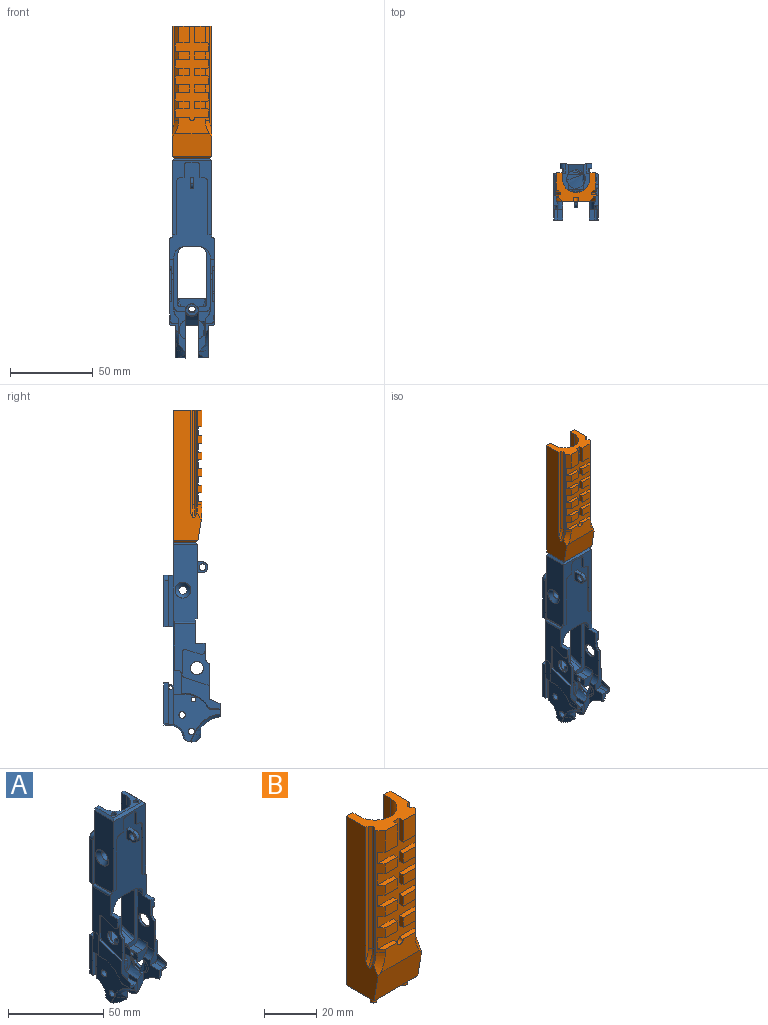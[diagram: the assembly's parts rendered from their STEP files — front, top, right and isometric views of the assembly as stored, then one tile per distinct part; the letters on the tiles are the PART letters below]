
ASSEMBLY  parts=2 mates=1
PART A: 257 faces, bbox 27.3x36.3x122.7 mm
  f0: plane 2.29x2.29mm, normal (0,0,-1), area 4.1mm2, adj f3
  f1: revolved ~2.45x2.45mm, area 5.5mm2, adj f7
  f2: plane 3.88x1.52mm, normal (0,-0.31,0.95), area 4.5mm2, adj f4,f9,f11,f15
  f3: revolved ~4.48x2.29mm, area 64.4mm2, adj f0,f16
  f4: revolved ~8.5x8.5mm, area 11.2mm2, adj f2,f11,f12,f15,f18,f21
  f5: plane 0.09x0.09mm, normal (0,-1,0), area 0mm2, adj f6,f20,f21
  f6: bspline ~6.22x2.03mm, area 0.6mm2, adj f5,f20,f21,f71
  f7: revolved ~2.74x2.45mm, area 42.1mm2, adj f1,f29
  f8: revolved ~4.17x4.17mm, area 7.3mm2, adj f28,f33
  f9: revolved ~8.3x5.57mm, area 28.9mm2, adj f2,f11,f15,f18,f35
  f10: plane 11.64x3.81mm, normal (0,-1,0), area 32mm2, adj f11,f35
  f11: revolved ~11.64x8.89mm, area 51.2mm2, adj f2,f4,f9,f10,f12,f35
  f12: plane 10.47x4.14mm, normal (0,-1,0), area 29.5mm2, adj f4,f11,f14,f20,f21,f35
  f13: plane 5.19x2.18mm, normal (0,-0.92,-0.39), area 0mm2, adj f14,f41
  f14: revolved ~6.77x5.98mm, area 26.7mm2, adj f12,f13,f20,f35,f42
  f15: plane 12.35x9.78mm, normal (-1,0,0), area 36.3mm2, adj f2,f4,f9,f18,f43,f44,f45,f46
  f16: plane 2.8x2.8mm, normal (0,0,-1), area 2mm2, adj f3,f51
  f17: revolved ~2.34x1.3mm, area 1.8mm2, adj f18,f35,f54
  f18: plane 4.58x4.03mm, normal (0,0.31,-0.95), area 12.7mm2, adj f4,f9,f15,f17,f21,f35,f54
  f19: plane 21.92x16.23mm, normal (1,0,0), area 223.2mm2, adj f52,f55,f62,f63,f64,f65,f66,f67
  f20: bspline ~15.82x13.1mm, area 51.2mm2, adj f5,f6,f12,f14,f21,f41,f71
  f21: plane 15.59x11.71mm, normal (-1,0,0), area 86.1mm2, adj f4,f5,f6,f12,f18,f20,f22,f53
  f22: plane 6.6x3.43mm, normal (0,0,1), area 22.6mm2, adj f21,f23,f69,f71
  f23: revolved ~6.6x1.59mm, area 16.5mm2, adj f22,f24,f69,f71
  f24: plane 6.6x3.63mm, normal (-1,0,0), area 14.7mm2, adj f23,f69,f70,f71
  f25: plane 0.09x0.09mm, normal (0,-1,0), area 0mm2, adj f26,f80,f81
  f26: bspline ~6.22x2.03mm, area 0.6mm2, adj f25,f80,f81,f144
  f27: revolved ~3.18x3.18mm, area 9.2mm2, adj f91
  f28: revolved ~5.17x4.64mm, area 59.5mm2, adj f8,f92
  f29: revolved ~2.96x2.96mm, area 4.3mm2, adj f7,f92
  f30: revolved ~3.68x3.68mm, area 5.5mm2, adj f91,f92
  f31: plane 2.54x0.16mm, normal (0,0.06,-1), area 0.3mm2, adj f36,f92,f93,f94
  f32: plane 21.91x16.23mm, normal (-1,0,0), area 223.2mm2, adj f56,f57,f104,f105,f106,f107,f108,f109
  f33: plane 7.97x7.9mm, normal (0,-0.99,-0.1), area 35.9mm2, adj f8,f88,f90,f114
  f34: plane 1.64x0.17mm, normal (0,-0.06,1), area 0.3mm2, adj f36,f37,f94,f118
  f35: plane 28.3x22.24mm, normal (-1,0,0), area 324.2mm2, adj f9,f10,f11,f12,f14,f17,f18,f36
  f36: revolved ~5.6x4.24mm, area 21mm2, adj f31,f34,f35,f92,f94,f119
  f37: bspline ~1.39x0.2mm, area 0.2mm2, adj f34,f118,f119,f194
  f38: revolved ~3.14x2.2mm, area 8.4mm2, adj f39,f50,f73,f121
  f39: plane 5.22x3.14mm, normal (0,0,-1), area 16.4mm2, adj f38,f71,f72,f121
  f40: revolved ~5.93x3.96mm, area 73.7mm2, adj f35,f41,f121
  f41: bspline ~17.88x17.13mm, area 10.9mm2, adj f13,f20,f40,f42,f71,f121
  f42: revolved ~10.38x5.93mm, area 47.7mm2, adj f14,f35,f41,f119,f120,f121
  f43: revolved ~5.2x3.49mm, area 13.3mm2, adj f15,f44,f47,f121
  f44: plane 4.69x1.59mm, normal (0,-0.31,0.95), area 7.8mm2, adj f15,f43,f45,f121
  f45: revolved ~4.76x3.49mm, area 11.8mm2, adj f15,f44,f46,f121
  f46: revolved ~5.22x2.62mm, area 10.6mm2, adj f15,f45,f47,f121
  f47: plane 1.59x0.3mm, normal (0,0.31,-0.95), area 0.5mm2, adj f15,f43,f46,f121
  f48: revolved ~5.93x2.79mm, area 104.1mm2, adj f35,f121
  f49: revolved ~5.93x4mm, area 74.5mm2, adj f35,f121
  f50: revolved ~13.78x7.99mm, area 52.3mm2, adj f38,f53,f54,f74,f121,f122
  f51: revolved ~26.67x2.79mm, area 234.1mm2, adj f16,f122
  f52: revolved ~3.68x2.44mm, area 6.1mm2, adj f19,f62,f69,f125
  f53: revolved ~5.32x5.08mm, area 32mm2, adj f21,f50,f54,f69,f121,f125
  f54: plane 9.02x7.01mm, normal (0,-1,0), area 33.2mm2, adj f17,f18,f21,f35,f50,f53,f114,f115
  f55: revolved ~7.95x7.95mm, area 32.7mm2, adj f19,f125
  f56: revolved ~3.68x2.44mm, area 6.1mm2, adj f32,f104,f111,f126
  f57: revolved ~7.95x7.95mm, area 32.7mm2, adj f32,f126
  f58: revolved ~3.18x3.18mm, area 11.7mm2, adj f59,f129,f130,f131
  f59: revolved ~3.18x3.18mm, area 11.7mm2, adj f58,f128,f129,f131
  f60: revolved ~4.04x4.04mm, area 29.6mm2, adj f129,f131
  f61: plane 7.14x0.51mm, normal (0.71,0,-0.71), area 4.9mm2, adj f74,f122,f123,f132
  f62: plane 8.51x2.57mm, normal (0,-1,0), area 16.8mm2, adj f19,f52,f63,f124,f125,f132
  f63: revolved ~4.57x4.55mm, area 23.5mm2, adj f19,f62,f64,f132
  f64: plane 8.72x2.83mm, normal (0,0.31,-0.95), area 11.5mm2, adj f19,f63,f65,f132
  f65: revolved ~2.08x1.59mm, area 3.8mm2, adj f19,f64,f66,f132
  f66: plane 13.89x1.26mm, normal (0,-1,0), area 17.5mm2, adj f19,f65,f67,f132
  f67: revolved ~1.51x1.26mm, area 2.5mm2, adj f19,f66,f68,f132
  f68: plane 15.13x4.92mm, normal (0,-0.31,0.95), area 20mm2, adj f19,f67,f69,f132
  f69: plane 26.8x5.45mm, normal (0,-1,0), area 62.3mm2, adj f19,f21,f22,f23,f24,f52,f53,f68
  f70: plane 6.6x2.8mm, normal (0,-0.39,0.92), area 3.1mm2, adj f24,f69,f71,f132
  f71: plane 8.06x5.46mm, normal (0,-1,0), area 14.2mm2, adj f6,f20,f21,f22,f23,f24,f39,f41
  f72: plane 5.22x0.51mm, normal (0.71,0,-0.71), area 3.8mm2, adj f39,f71,f73,f132
  f73: revolved ~2.2x1.53mm, area 1.7mm2, adj f38,f72,f74,f132
  f74: revolved ~14.22x8.5mm, area 12.2mm2, adj f50,f61,f73,f132
  f75: revolved ~5.32x5.08mm, area 32mm2, adj f80,f104,f126,f141,f147,f218
  f76: plane 5.19x2.18mm, normal (0,-0.92,-0.39), area 0mm2, adj f87,f143,f152
  f77: plane 6.6x3.63mm, normal (1,0,0), area 14.7mm2, adj f78,f103,f104,f144
  f78: revolved ~6.6x1.59mm, area 16.5mm2, adj f77,f79,f104,f144
  f79: plane 6.6x3.43mm, normal (0,0,1), area 22.6mm2, adj f78,f80,f104,f144
  f80: plane 15.59x11.71mm, normal (1,0,0), area 109mm2, adj f25,f26,f75,f79,f81,f104,f141,f144
  f81: bspline ~15.82x13.1mm, area 51.2mm2, adj f25,f26,f80,f87,f141,f143,f144
  f82: plane 2.54x0.16mm, normal (0,0.06,-1), area 0.3mm2, adj f92,f95,f150,f158
  f83: revolved ~9.49x8.73mm, area 81.8mm2, adj f35,f86,f114,f151
  f84: plane 11.64x3.81mm, normal (0,-1,0), area 32mm2, adj f85,f151
  f85: revolved ~11.64x8.89mm, area 130.9mm2, adj f84,f141,f151
  f86: plane 7.87x1.38mm, normal (0,0,-1), area 10.9mm2, adj f35,f83,f92,f151
  f87: revolved ~6.77x5.98mm, area 26.7mm2, adj f76,f81,f141,f151,f152
  f88: revolved ~1.99x0.92mm, area 0.1mm2, adj f33,f89,f155
  f89: plane 5.19x0.92mm, normal (0,0.99,0.1), area 3.4mm2, adj f88,f90,f155
  f90: revolved ~1.99x0.92mm, area 0.1mm2, adj f33,f89,f155
  f91: revolved ~7.94x3.18mm, area 72mm2, adj f27,f30,f155
  f92: plane 25.55x19.4mm, normal (0,1,0), area 383.5mm2, adj f28,f29,f30,f31,f35,f36,f82,f86
  f93: plane 24.86x2.54mm, normal (1,0,0), area 62.9mm2, adj f31,f92,f94,f157
  f94: plane 25.15x1.86mm, normal (0,-1,0), area 45.9mm2, adj f31,f34,f36,f93,f117,f118,f157
  f95: plane 24.86x2.54mm, normal (-1,0,0), area 62.9mm2, adj f82,f92,f157,f158
  f96: plane 6.99x3.84mm, normal (0,0,1), area 26.6mm2, adj f99,f114,f141,f162
  f97: plane 2.97x1.89mm, normal (1,0,0), area 2.9mm2, adj f98,f114,f162
  f98: revolved ~2.97x1.57mm, area 1.3mm2, adj f97,f114,f162
  f99: revolved ~6.99x3.18mm, area 34.8mm2, adj f96,f126,f141,f162
  f100: revolved ~14.22x8.5mm, area 12.2mm2, adj f101,f140,f147,f167
  f101: revolved ~2.2x1.53mm, area 1.7mm2, adj f100,f102,f146,f167
  f102: plane 5.22x0.51mm, normal (-0.71,0,-0.71), area 3.8mm2, adj f101,f144,f145,f167
  f103: plane 6.6x2.8mm, normal (0,-0.39,0.92), area 3.1mm2, adj f77,f104,f144,f167
  f104: plane 26.8x5.45mm, normal (0,-1,0), area 62.3mm2, adj f32,f56,f75,f77,f78,f79,f80,f103
  f105: plane 15.13x4.92mm, normal (0,-0.31,0.95), area 20mm2, adj f32,f104,f106,f167
  f106: revolved ~1.51x1.26mm, area 2.5mm2, adj f32,f105,f107,f167
  f107: plane 13.89x1.26mm, normal (0,-1,0), area 17.5mm2, adj f32,f106,f108,f167
  f108: revolved ~2.08x1.59mm, area 3.8mm2, adj f32,f107,f109,f167
  f109: plane 8.72x2.83mm, normal (0,0.31,-0.95), area 11.5mm2, adj f32,f108,f110,f167
  f110: revolved ~2.99x2.29mm, area 5.4mm2, adj f32,f109,f111,f167
  f111: plane 8.51x2.57mm, normal (0,-1,0), area 16.8mm2, adj f32,f56,f110,f126,f127,f167
  f112: revolved ~2.97x1.57mm, area 1.3mm2, adj f113,f114,f188
  f113: plane 2.97x1.89mm, normal (-1,0,0), area 2.9mm2, adj f112,f114,f188
  f114: revolved ~18.31x9.73mm, area 158.1mm2, adj f33,f35,f54,f83,f96,f97,f98,f112
  f115: plane 6.99x3.84mm, normal (0,0,1), area 26.6mm2, adj f54,f114,f116,f188
  f116: revolved ~6.99x3.18mm, area 34.8mm2, adj f54,f115,f125,f188
  f117: revolved ~15.25x6.17mm, area 29.5mm2, adj f94,f118,f156,f157,f187,f188,f194
  f118: plane 24.96x3.04mm, normal (1,0,0), area 69mm2, adj f34,f37,f94,f117,f155,f194
  f119: bspline ~9.13x8.49mm, area 68.2mm2, adj f35,f36,f37,f42,f120,f194
  f120: revolved ~8.86x6.86mm, area 4mm2, adj f42,f119,f121,f194
  f121: plane 28.95x28.4mm, normal (1,0,0), area 358.4mm2, adj f38,f39,f40,f41,f42,f43,f44,f45
  f122: plane 7.14x3.14mm, normal (0,0,-1), area 16.3mm2, adj f50,f51,f61,f121,f194
  f123: plane 31.7x0.51mm, normal (0.71,0.71,0), area 22.6mm2, adj f61,f132,f194,f198
  f124: plane 5.82x2.57mm, normal (0,0,1), area 14.9mm2, adj f62,f125,f132,f201
  f125: plane 32.09x12.07mm, normal (-1,0,0), area 283.8mm2, adj f52,f53,f54,f55,f62,f69,f116,f124
  f126: plane 32.09x12.07mm, normal (1,0,0), area 283.8mm2, adj f56,f57,f75,f99,f104,f111,f127,f141
  f127: plane 5.82x2.57mm, normal (0,0,1), area 14.9mm2, adj f111,f126,f167,f201
  f128: plane 4.32x2.34mm, normal (0,0,1), area 10.1mm2, adj f59,f129,f131,f201
  f129: plane 7.5x6.35mm, normal (-1,0,0), area 30.4mm2, adj f58,f59,f60,f128,f130,f201
  f130: plane 4.32x2.34mm, normal (0,0,-1), area 10.1mm2, adj f58,f129,f131,f201
  f131: plane 7.5x6.35mm, normal (1,0,0), area 30.4mm2, adj f58,f59,f60,f128,f130,f201
  f132: plane 51.57x27.84mm, normal (1,0,0), area 473.8mm2, adj f61,f62,f63,f64,f65,f66,f67,f68
  f133: revolved ~4.27x1.27mm, area 8.4mm2, adj f132,f201,f202,f203
  f134: plane 5.93x0.85mm, normal (0,0,1), area 3.4mm2, adj f210,f211
  f135: revolved ~6.35x6.33mm, area 26.6mm2, adj f212,f213,f214,f215
  f136: plane 9.47x1.91mm, normal (0,0.71,0.71), area 25.5mm2, adj f137,f192,f211,f216
  f137: plane 9.47x6.1mm, normal (0,0,1), area 57.8mm2, adj f136,f211,f215,f216
  f138: plane 5.93x0.85mm, normal (0,0,1), area 3.4mm2, adj f205,f216
  f139: revolved ~5.11x5.11mm, area 78mm2, adj f171,f216
  f140: plane 2.31x0.51mm, normal (-0.71,0,-0.71), area 1.7mm2, adj f100,f167,f169,f217
  f141: plane 27.95x7.02mm, normal (0,-1,0), area 70.4mm2, adj f75,f80,f81,f85,f87,f96,f99,f114
  f142: revolved ~5.93x3.96mm, area 73.7mm2, adj f143,f151,f218
  f143: bspline ~18.1x17.29mm, area 10.9mm2, adj f76,f81,f142,f144,f152,f218
  f144: plane 8.06x5.46mm, normal (0,-1,0), area 14.2mm2, adj f26,f77,f78,f79,f80,f81,f102,f103
  f145: plane 5.22x3.14mm, normal (0,0,-1), area 16.4mm2, adj f102,f144,f146,f218
  f146: revolved ~3.14x2.2mm, area 8.4mm2, adj f101,f145,f147,f218
  f147: revolved ~13.78x7.99mm, area 52.3mm2, adj f75,f100,f141,f146,f217,f218
  f148: revolved ~5.93x4mm, area 74.5mm2, adj f151,f218
  f149: revolved ~5.93x2.79mm, area 52.1mm2, adj f151,f218
  f150: revolved ~5.6x4.24mm, area 21mm2, adj f82,f92,f151,f153,f158,f220
  f151: plane 28.3x22.24mm, normal (1,0,0), area 325.4mm2, adj f83,f84,f85,f86,f87,f92,f114,f141
  f152: revolved ~10.38x5.93mm, area 48mm2, adj f76,f87,f143,f151,f218,f219,f220
  f153: plane 1.64x0.17mm, normal (0,-0.06,1), area 0.3mm2, adj f150,f154,f158,f221
  f154: bspline ~1.39x0.2mm, area 0.2mm2, adj f153,f220,f221,f245
  f155: revolved ~15.62x2.36mm, area 104.7mm2, adj f88,f89,f90,f91,f114,f118,f221
  f156: plane 14.78x14.28mm, normal (0,-0.3,0.95), area 197.1mm2, adj f114,f117,f157,f162,f188,f222
  f157: plane 19.3x2.54mm, normal (0,0,1), area 15.7mm2, adj f92,f93,f94,f95,f117,f156,f158,f222
  f158: plane 25.15x1.86mm, normal (0,-1,0), area 45.9mm2, adj f82,f95,f150,f153,f157,f221,f222
  f159: revolved ~0.31x0.26mm, area 0mm2, adj f206,f216,f224
  f160: plane 1.5x1.42mm, normal (0,0,-1), area 0.7mm2, adj f161,f201,f224
  f161: revolved ~6.03x6.03mm, area 34.2mm2, adj f126,f160,f162,f201,f224
  f162: plane 39.26x8.3mm, normal (0,-1,0), area 96.8mm2, adj f96,f97,f98,f99,f114,f126,f156,f161
  f163: plane 30.87x1.84mm, normal (0,-1,0), area 55.5mm2, adj f164,f165,f225,f226,f227
  f164: plane 28.07x2.54mm, normal (-1,0,0), area 71.3mm2, adj f163,f207,f225,f227
  f165: plane 3.02x0.17mm, normal (0,0,-1), area 0.5mm2, adj f163,f226,f227,f245
  f166: revolved ~12.98x1.27mm, area 25.9mm2, adj f167,f170,f201,f229
  f167: plane 51.57x27.84mm, normal (-1,0,0), area 506.7mm2, adj f100,f101,f102,f103,f104,f105,f106,f107
  f168: revolved ~1.59x1.59mm, area 2.2mm2, adj f167,f169,f231,f232
  f169: plane 12.76x0.89mm, normal (0,1,0), area 11.2mm2, adj f140,f167,f168,f217,f232
  f170: plane 12.98x0.43mm, normal (0,0,1), area 5.6mm2, adj f166,f201,f228,f233
  f171: revolved ~9.53x9.53mm, area 71.8mm2, adj f139,f233
  f172: plane 31.5x1.12mm, normal (-1,0,0), area 35.2mm2, adj f173,f200,f201,f234
  f173: revolved ~3.18x3.18mm, area 5.6mm2, adj f172,f174,f201,f234
  f174: plane 1.71x1.12mm, normal (0,0,-1), area 1.9mm2, adj f173,f175,f201,f234
  f175: plane 7.3x1.12mm, normal (-1,0,0), area 8.2mm2, adj f174,f176,f201,f234
  f176: revolved ~1.59x1.59mm, area 2.8mm2, adj f175,f177,f201,f234
  f177: plane 6.35x1.12mm, normal (0,0,-1), area 7.1mm2, adj f176,f178,f201,f234
  f178: revolved ~1.59x1.59mm, area 2.8mm2, adj f177,f179,f201,f234
  f179: plane 7.3x1.12mm, normal (1,0,0), area 8.2mm2, adj f178,f180,f201,f234
  f180: plane 1.71x1.12mm, normal (0,0,-1), area 1.9mm2, adj f179,f181,f201,f234
  f181: revolved ~3.18x3.18mm, area 5.6mm2, adj f180,f182,f201,f234
  f182: plane 31.5x1.12mm, normal (1,0,0), area 35.2mm2, adj f181,f183,f201,f234
  f183: plane 2.16x1.12mm, normal (0,0,-1), area 2.4mm2, adj f182,f201,f233,f234
  f184: plane 3.02x0.17mm, normal (0,0,-1), area 0.5mm2, adj f185,f235,f236,f249
  f185: plane 30.87x1.84mm, normal (0,-1,0), area 55.5mm2, adj f184,f186,f235,f236,f237
  f186: plane 28.07x2.54mm, normal (1,0,0), area 71.3mm2, adj f185,f208,f235,f237
  f187: plane 30.43x9.68mm, normal (-1,0,0), area 265.5mm2, adj f117,f188,f194,f195,f196,f238
  f188: plane 39.26x8.3mm, normal (0,-1,0), area 96.8mm2, adj f112,f113,f114,f115,f116,f117,f125,f156
  f189: revolved ~6.03x6.03mm, area 34.2mm2, adj f125,f188,f190,f201,f238
  f190: plane 1.5x1.42mm, normal (0,0,-1), area 0.7mm2, adj f189,f201,f238
  f191: plane 11.43x4.75mm, normal (0,0.3,-0.95), area 56.9mm2, adj f192,f201,f224,f238
  f192: plane 9.55x4.37mm, normal (0,1,0), area 36.9mm2, adj f136,f191,f211,f216,f224,f238
  f193: revolved ~0.31x0.26mm, area 0mm2, adj f209,f211,f238
  f194: plane 50.92x5.28mm, normal (0,1,0), area 179.4mm2, adj f37,f117,f118,f119,f120,f121,f122,f123
  f195: plane 5.87x0.76mm, normal (0,0,1), area 4.5mm2, adj f187,f194,f196,f240
  f196: plane 6.73x2.61mm, normal (0,1,0), area 7.5mm2, adj f187,f195,f238,f239,f240
  f197: revolved ~4.03x1.58mm, area 9.6mm2, adj f132,f198,f203,f240
  f198: plane 6.96x4.03mm, normal (0,0,1), area 27.9mm2, adj f123,f132,f194,f197,f240
  f199: revolved ~5.11x5.11mm, area 76.2mm2, adj f211,f240
  f200: plane 2.16x1.12mm, normal (0,0,-1), area 2.4mm2, adj f172,f201,f234,f242
  f201: plane 58.44x27.05mm, normal (0,-1,0), area 979.5mm2, adj f124,f125,f126,f127,f128,f129,f130,f131
  f202: plane 4.18x0.43mm, normal (0,0,1), area 1.8mm2, adj f133,f201,f203,f242
  f203: plane 29.06x4.07mm, normal (0,1,0.07), area 85.9mm2, adj f132,f133,f197,f202,f204,f240,f242
  f204: revolved ~6.79x6.35mm, area 24.2mm2, adj f203,f240,f241,f242
  f205: revolved ~5.93x3.81mm, area 23.8mm2, adj f138,f216,f243
  f206: revolved ~28.34x0.81mm, area 28.1mm2, adj f159,f207,f216,f224,f243
  f207: plane 31.37x4.23mm, normal (0,1,0), area 121.7mm2, adj f164,f206,f224,f225,f227,f243
  f208: plane 31.37x4.23mm, normal (0,1,0), area 121.7mm2, adj f186,f209,f235,f237,f238,f243
  f209: revolved ~28.34x0.81mm, area 28.1mm2, adj f193,f208,f211,f238,f243
  f210: revolved ~5.93x3.81mm, area 23.8mm2, adj f134,f211,f243
  f211: plane 30.34x15.04mm, normal (-1,0,0), area 357.6mm2, adj f134,f136,f137,f192,f193,f199,f209,f210
  f212: plane 13.78x0.89mm, normal (-1,0,0), area 12.2mm2, adj f135,f213,f215,f243
  f213: plane 16.96x6.35mm, normal (0,1,0), area 103.3mm2, adj f135,f212,f214,f243
  f214: plane 13.78x0.89mm, normal (1,0,0), area 12.2mm2, adj f135,f213,f215,f243
  f215: plane 24.13x9.48mm, normal (0,1,0), area 125.3mm2, adj f135,f137,f211,f212,f214,f216,f243
  f216: plane 30.34x15.04mm, normal (1,0,0), area 357.6mm2, adj f136,f137,f138,f139,f159,f192,f205,f206
  f217: plane 7.14x3.14mm, normal (0,0,-1), area 20.6mm2, adj f140,f147,f169,f218,f232,f245
  f218: plane 28.95x28.4mm, normal (-1,0,0), area 413.9mm2, adj f75,f141,f142,f143,f144,f145,f146,f147
  f219: revolved ~8.86x6.86mm, area 4mm2, adj f152,f218,f220,f245
  f220: bspline ~9.06x8.27mm, area 68.2mm2, adj f150,f151,f152,f154,f219,f245
  f221: plane 24.96x3.04mm, normal (-1,0,0), area 69mm2, adj f153,f154,f155,f158,f222,f245
  f222: revolved ~15.25x6.17mm, area 29.5mm2, adj f156,f157,f158,f162,f221,f223,f245
  f223: plane 32.28x9.68mm, normal (1,0,0), area 282.9mm2, adj f162,f222,f224,f245
  f224: revolved ~20.75x12mm, area 129.2mm2, adj f159,f160,f161,f162,f191,f192,f201,f206
  f225: plane 5.86x3.01mm, normal (0,0,-1), area 5.9mm2, adj f163,f164,f207,f224,f226,f245
  f226: plane 30.87x3.02mm, normal (-1,0,0), area 93.3mm2, adj f163,f165,f225,f245
  f227: revolved ~5.56x3.18mm, area 17.4mm2, adj f163,f164,f165,f207,f243,f245
  f228: plane 0.51x0.51mm, normal (0,0.71,0.71), area 0.3mm2, adj f170,f229,f233,f245
  f229: revolved ~1.27x1.27mm, area 1.1mm2, adj f166,f228,f230,f245
  f230: plane 28.45x0.51mm, normal (-0.71,0.71,0), area 20.4mm2, adj f167,f229,f231,f245
  f231: plane 3.24x0.89mm, normal (0,0,-1), area 2.7mm2, adj f167,f168,f230,f232,f245
  f232: plane 14.35x4.83mm, normal (-1,0,0), area 68.7mm2, adj f168,f169,f217,f231,f245
  f233: plane 46.99x14.61mm, normal (-1,0,0), area 605.9mm2, adj f170,f171,f183,f201,f228,f234,f245,f246
  f234: plane 44.83x23.63mm, normal (0,-1,0), area 310.5mm2, adj f172,f173,f174,f175,f176,f177,f178,f179
  f235: revolved ~5.56x3.18mm, area 17.4mm2, adj f184,f185,f186,f208,f243,f249
  f236: plane 30.87x3.02mm, normal (1,0,0), area 93.3mm2, adj f184,f185,f237,f249
  f237: plane 5.86x3.01mm, normal (0,0,-1), area 5.9mm2, adj f185,f186,f208,f236,f238,f249
  f238: revolved ~20.75x12mm, area 106.1mm2, adj f187,f188,f189,f190,f191,f192,f193,f196
  f239: plane 6.19x2.83mm, normal (0,0,-1), area 10.8mm2, adj f196,f238,f240,f249
  f240: plane 37.29x10.6mm, normal (1,0,0), area 293.4mm2, adj f194,f195,f196,f197,f198,f199,f203,f204
  f241: plane 4.24x2.32mm, normal (0,0,-1), area 9.9mm2, adj f204,f240,f242,f249
  f242: plane 46.48x14.61mm, normal (1,0,0), area 433.6mm2, adj f200,f201,f202,f203,f204,f234,f241,f248
  f243: plane 17.53x16.72mm, normal (0,0,1), area 81.1mm2, adj f205,f206,f207,f208,f209,f210,f211,f212
  f244: plane 2.64x2.64mm, normal (0,0,1), area 5.5mm2, adj f253
  f245: plane 110.56x6.64mm, normal (0,1,0), area 410.8mm2, adj f154,f165,f217,f218,f219,f220,f221,f222
  f246: plane 14.61x1.27mm, normal (-0.71,0,0.71), area 25.1mm2, adj f233,f245,f247,f255
  f247: plane 23.62x1.27mm, normal (0,-0.71,0.71), area 40.1mm2, adj f234,f246,f248,f255
  f248: plane 14.61x1.27mm, normal (0.71,0,0.71), area 25.1mm2, adj f242,f247,f249,f255
  f249: plane 53.03x5.37mm, normal (0,1,0), area 130.7mm2, adj f184,f235,f236,f237,f238,f239,f240,f241
  f250: plane 19.86x3.61mm, normal (-1,0,0), area 71.6mm2, adj f243,f249,f251,f255
  f251: revolved ~19.86x16.71mm, area 521.5mm2, adj f243,f250,f252,f255
  f252: plane 19.86x3.61mm, normal (1,0,0), area 71.6mm2, adj f243,f245,f251,f255
  f253: revolved ~3.05x2.64mm, area 50.6mm2, adj f244,f255
  f254: plane 2.64x2.64mm, normal (0,0,1), area 5.5mm2, adj f256
  f255: plane 21.08x13.34mm, normal (0,0,1), area 100.2mm2, adj f245,f246,f247,f248,f249,f250,f251,f252
  f256: revolved ~3.05x2.64mm, area 25.3mm2, adj f254,f255
PART B: 84 faces, bbox 33.5x23.6x89.2 mm
  f0: plane 2.54x2.54mm, normal (0,0,-1), area 5.1mm2, adj f2
  f1: plane 2.54x2.54mm, normal (0,0,-1), area 5.1mm2, adj f3
  f2: revolved ~2.54x2.54mm, area 20.3mm2, adj f0,f8
  f3: revolved ~2.54x2.54mm, area 20.3mm2, adj f1,f8
  f4: revolved ~7.83x3.41mm, area 11.8mm2, adj f5,f13,f38,f39
  f5: revolved ~7.83x2.41mm, area 10.6mm2, adj f4,f6,f14,f39
  f6: revolved ~7.83x3.41mm, area 11.8mm2, adj f5,f15,f16,f39
  f7: plane 14.94x1.27mm, normal (0.71,0,-0.71), area 25.7mm2, adj f8,f17,f39,f40
  f8: plane 21.08x13.67mm, normal (0,0,-1), area 108mm2, adj f2,f3,f7,f10,f17,f18,f19,f20
  f9: revolved ~7.83x2.41mm, area 10.6mm2, adj f11,f12,f24,f41
  f10: plane 14.94x1.27mm, normal (-0.71,0,-0.71), area 25.7mm2, adj f8,f21,f40,f41
  f11: revolved ~7.83x3.41mm, area 11.8mm2, adj f9,f22,f23,f41
  f12: revolved ~7.83x3.41mm, area 11.8mm2, adj f9,f25,f41,f42
  f13: plane 57.15x1.21mm, normal (0.71,0.71,0), area 97.5mm2, adj f4,f14,f36,f69
  f14: plane 57.15x1.27mm, normal (1,0,0), area 72.6mm2, adj f5,f13,f15,f69
  f15: plane 57.15x1.21mm, normal (0.71,-0.71,0), area 97.5mm2, adj f6,f14,f16,f69
  f16: plane 62.56x1.21mm, normal (0,-1,0), area 73.3mm2, adj f6,f15,f39,f69
  f17: plane 80.26x3.45mm, normal (0,1,0), area 276.5mm2, adj f7,f8,f18,f39,f69
  f18: plane 80.26x3.61mm, normal (-1,0,0), area 289.5mm2, adj f8,f17,f19,f69
  f19: revolved ~80.26x16.71mm, area 2107.2mm2, adj f8,f18,f20,f69
  f20: plane 80.26x3.61mm, normal (1,0,0), area 289.5mm2, adj f8,f19,f21,f69
  f21: plane 80.26x3.45mm, normal (0,1,0), area 276.5mm2, adj f8,f10,f20,f41,f69
  f22: plane 62.56x1.21mm, normal (0,-1,0), area 73.3mm2, adj f11,f23,f41,f69
  f23: plane 57.15x1.21mm, normal (-0.71,-0.71,0), area 97.5mm2, adj f11,f22,f24,f69
  f24: plane 57.15x1.27mm, normal (-1,0,0), area 72.6mm2, adj f9,f23,f25,f69
  f25: plane 57.15x1.21mm, normal (-0.71,0.71,0), area 97.5mm2, adj f12,f24,f29,f69
  f26: plane 6.49x4.67mm, normal (0,-1,0), area 30.3mm2, adj f46,f47,f48,f73
  f27: plane 6.49x4.67mm, normal (0,-1,0), area 30.3mm2, adj f49,f50,f51,f73
  f28: plane 6.49x4.67mm, normal (0,-1,0), area 30.3mm2, adj f52,f53,f54,f73
  f29: plane 57.15x0.53mm, normal (-1,0,0), area 30.5mm2, adj f25,f42,f69,f73
  f30: plane 10.16x6.49mm, normal (0,-1,0), area 65.9mm2, adj f69,f70,f71,f73
  f31: plane 6.49x4.67mm, normal (0,-1,0), area 30.3mm2, adj f43,f44,f45,f73
  f32: plane 6.49x4.67mm, normal (0,-1,0), area 30.3mm2, adj f58,f59,f60,f75
  f33: plane 6.49x4.67mm, normal (0,-1,0), area 30.3mm2, adj f61,f62,f63,f75
  f34: plane 6.49x4.67mm, normal (0,-1,0), area 30.3mm2, adj f64,f65,f66,f75
  f35: plane 10.16x6.49mm, normal (0,-1,0), area 65.9mm2, adj f67,f68,f69,f75
  f36: plane 57.15x0.53mm, normal (1,0,0), area 30.5mm2, adj f13,f38,f69,f75
  f37: plane 6.49x4.67mm, normal (0,-1,0), area 30.3mm2, adj f55,f56,f57,f75
  f38: revolved ~5.4x1.21mm, area 3mm2, adj f4,f36,f39,f76
  f39: plane 79.47x17.5mm, normal (1,0,0), area 914.5mm2, adj f4,f5,f6,f7,f16,f17,f38,f40
  f40: plane 23.62x1.29mm, normal (0,-0.71,-0.71), area 40.6mm2, adj f7,f8,f10,f39,f41,f77
  f41: plane 79.47x17.5mm, normal (-1,0,0), area 914.5mm2, adj f9,f10,f11,f12,f21,f22,f40,f42
  f42: revolved ~5.4x1.21mm, area 3mm2, adj f12,f29,f41,f78
  f43: plane 8.65x2.16mm, normal (0,0,1), area 16.3mm2, adj f31,f44,f73,f80
  f44: plane 4.67x2.16mm, normal (1,0,0), area 10.1mm2, adj f31,f43,f45,f80
  f45: plane 8.65x2.16mm, normal (0,0,-1), area 16.3mm2, adj f31,f44,f73,f80
  f46: plane 8.65x2.16mm, normal (0,0,1), area 16.3mm2, adj f26,f47,f73,f80
  f47: plane 4.67x2.16mm, normal (1,0,0), area 10.1mm2, adj f26,f46,f48,f80
  f48: plane 8.65x2.16mm, normal (0,0,-1), area 16.3mm2, adj f26,f47,f73,f80
  f49: plane 8.65x2.16mm, normal (0,0,1), area 16.3mm2, adj f27,f50,f73,f80
  f50: plane 4.67x2.16mm, normal (1,0,0), area 10.1mm2, adj f27,f49,f51,f80
  f51: plane 8.65x2.16mm, normal (0,0,-1), area 16.3mm2, adj f27,f50,f73,f80
  f52: plane 8.65x2.16mm, normal (0,0,1), area 16.3mm2, adj f28,f53,f73,f80
  f53: plane 4.67x2.16mm, normal (1,0,0), area 10.1mm2, adj f28,f52,f54,f80
  f54: plane 8.65x2.16mm, normal (0,0,-1), area 16.3mm2, adj f28,f53,f73,f80
  f55: plane 8.65x2.16mm, normal (0,0,-1), area 16.3mm2, adj f37,f56,f75,f80
  f56: plane 4.67x2.16mm, normal (-1,0,0), area 10.1mm2, adj f37,f55,f57,f80
  f57: plane 8.65x2.16mm, normal (0,0,1), area 16.3mm2, adj f37,f56,f75,f80
  f58: plane 8.65x2.16mm, normal (0,0,-1), area 16.3mm2, adj f32,f59,f75,f80
  f59: plane 4.67x2.16mm, normal (-1,0,0), area 10.1mm2, adj f32,f58,f60,f80
  f60: plane 8.65x2.16mm, normal (0,0,1), area 16.3mm2, adj f32,f59,f75,f80
  f61: plane 8.65x2.16mm, normal (0,0,-1), area 16.3mm2, adj f33,f62,f75,f80
  f62: plane 4.67x2.16mm, normal (-1,0,0), area 10.1mm2, adj f33,f61,f63,f80
  f63: plane 8.65x2.16mm, normal (0,0,1), area 16.3mm2, adj f33,f62,f75,f80
  f64: plane 8.65x2.16mm, normal (0,0,-1), area 16.3mm2, adj f34,f65,f75,f80
  f65: plane 4.67x2.16mm, normal (-1,0,0), area 10.1mm2, adj f34,f64,f66,f80
  f66: plane 8.65x2.16mm, normal (0,0,1), area 16.3mm2, adj f34,f65,f75,f80
  f67: plane 8.65x2.16mm, normal (0,0,-1), area 16.3mm2, adj f35,f68,f75,f80
  f68: plane 10.16x2.16mm, normal (-1,0,0), area 21.9mm2, adj f35,f67,f69,f80
  f69: plane 23.62x17.27mm, normal (0,0,1), area 202.5mm2, adj f13,f14,f15,f16,f17,f18,f19,f20
  f70: plane 10.16x2.16mm, normal (1,0,0), area 21.9mm2, adj f30,f69,f71,f80
  f71: plane 8.65x2.16mm, normal (0,0,-1), area 16.3mm2, adj f30,f70,f73,f80
  f72: plane 8.51x6.39mm, normal (1,0,0), area 0.1mm2, adj f74,f80,f81,f83
  f73: plane 57.15x2.53mm, normal (-0.71,-0.71,0), area 122.8mm2, adj f26,f27,f28,f29,f30,f31,f43,f45
  f74: plane 8.65x2.16mm, normal (0,0,1), area 16.3mm2, adj f72,f73,f80,f81
  f75: plane 57.15x2.53mm, normal (0.71,-0.71,0), area 122.8mm2, adj f32,f33,f34,f35,f36,f37,f55,f57
  f76: revolved ~9.77x5.48mm, area 28.8mm2, adj f38,f39,f75,f77,f81
  f77: plane 23.63x13.68mm, normal (0,-0.99,-0.17), area 325.5mm2, adj f39,f40,f41,f76,f78,f81
  f78: revolved ~9.77x5.48mm, area 28.8mm2, adj f41,f42,f73,f77,f81
  f79: plane 8.65x2.16mm, normal (0,0,1), area 16.3mm2, adj f75,f80,f81,f82
  f80: plane 63.5x26.82mm, normal (0,-1,0), area 641.6mm2, adj f43,f44,f45,f46,f47,f48,f49,f50
  f81: plane 27.24x16.13mm, normal (0,-1,0), area 166.4mm2, adj f72,f73,f74,f75,f76,f77,f78,f79
  f82: plane 8.51x6.39mm, normal (-1,0,0), area 0.1mm2, adj f79,f80,f81,f83
  f83: revolved ~3.18x3.17mm, area 21.5mm2, adj f72,f80,f81,f82
PLACE A t=(160.73,118.72,84.18)mm
PLACE B t=(148.92,124.59,113.03)mm
MATE parallel B.f8 <-> A.f255  axis (0,0,1) through (160.73,112.62,113.03)mm
